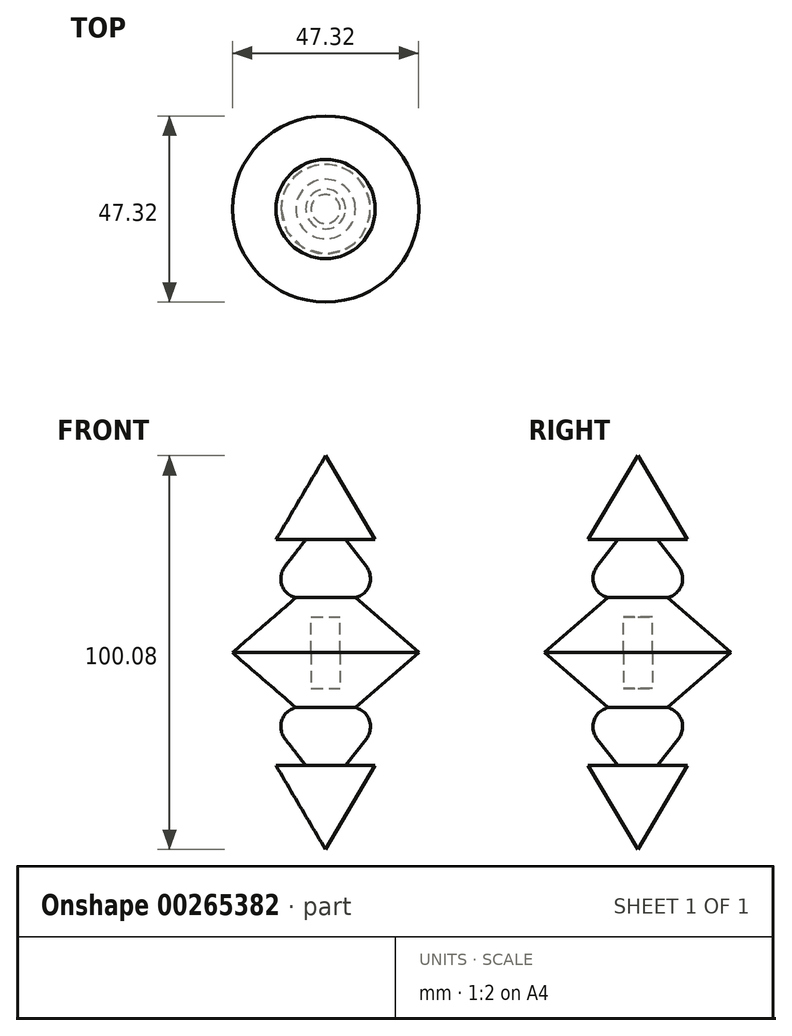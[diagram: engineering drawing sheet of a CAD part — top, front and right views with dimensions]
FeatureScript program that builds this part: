
annotation { "Feature Type Name" : "Feature", "Feature Type Description" : "" }
export const myFeature = defineFeature(function(context is Context, id is Id, definition is map)
    precondition{}
    {
        {
            var Q0;
            Q0=qCreatedBy(makeId("Front.planeOp"),FACE);
            var sketch = newSketch(context, id + "F0", { "sketchPlane" : qUnion([Q0])});
            skLineSegment(sketch, "E0", {"start": v(0, 50.04) * mm, "end": v(12.6, 28.7) * mm});
            skLineSegment(sketch, "E1", {"start": v(12.6, 28.7) * mm, "end": v(5.04, 28.7) * mm});
            skLineSegment(sketch, "E2", {"start": v(5.04, 28.7) * mm, "end": v(16.49, 13.97) * mm});
            skLineSegment(sketch, "E3", {"start": v(16.49, 13.97) * mm, "end": v(7.56, 13.97) * mm});
            skLineSegment(sketch, "E4", {"start": v(7.56, 13.97) * mm, "end": v(23.66, 0) * mm});
            skLineSegment(sketch, "E5", {"start": v(23.66, 0) * mm, "end": v(3.69, 0) * mm});
            skLineSegment(sketch, "E6", {"start": v(3.69, 0) * mm, "end": v(3.69, -9.12) * mm});
            skLineSegment(sketch, "E7", {"start": v(3.69, -9.12) * mm, "end": v(0, -9.12) * mm});
            skLineSegment(sketch, "E8", {"start": v(0, -9.12) * mm, "end": v(0, 50.04) * mm});
            skPoint(sketch, "E9.orphan", {"position": v(0, 0) * mm});
            skSolve(sketch);
        }
        {
            var Q0;
            Q0 = qSketchRegion(id + "F0", true);
            var Q1;
            Q1=sQuery(id+"F0.wireOp",EDGE,"E8");
            revolve(context, id + "F1", {"entities" : qUnion([Q0]), "axis" : qUnion([Q1]), "revolveType" : RevolveType.FULL});
        }
        {
            var Q0;
            Q0=makeQuery(id+"F1.opRevolve","SWEPT_BODY",BODY,{"disambiguationData":[OSD([sQuery(id+"F0.wireOp",EDGE,"E0"),sQuery(id+"F0.wireOp",EDGE,"E1"),sQuery(id+"F0.wireOp",EDGE,"E2"),sQuery(id+"F0.wireOp",EDGE,"E3"),sQuery(id+"F0.wireOp",EDGE,"E4"),sQuery(id+"F0.wireOp",EDGE,"E5"),sQuery(id+"F0.wireOp",EDGE,"E6"),sQuery(id+"F0.wireOp",EDGE,"E7"),sQuery(id+"F0.wireOp",EDGE,"E8")])]});
            var Q1;
            Q1=qCreatedBy(makeId("Top.planeOp"),FACE);
            mirror(context, id + "F2", {"entities" : qUnion([Q0]), "mirrorPlane" : qUnion([Q1])});
        }
        {
            var Q0;
            Q0=makeQuery(id+"F1.opRevolve","SWEPT_EDGE",EDGE,{"disambiguationData":[OSD([sQuery(id+"F0.wireOp",EDGE,"E2"),sQuery(id+"F0.wireOp",EDGE,"E3")])]});
            fillet(context, id + "F3", {"entities" : qUnion([Q0]), "radius" : 5 * mm, "tangentPropagation" : true, "allowEdgeOverflow" : false});
        }
        {
            var Q0;
            Q0=makeQuery(id+"F2.opPattern","COPY",EDGE,{"derivedFrom":makeQuery(id+"F1.opRevolve","SWEPT_EDGE",EDGE,{"disambiguationData":[OSD([sQuery(id+"F0.wireOp",EDGE,"E2"),sQuery(id+"F0.wireOp",EDGE,"E3")])]}),"instanceName":"1"});
            fillet(context, id + "F4", {"entities" : qUnion([Q0]), "radius" : 5 * mm, "tangentPropagation" : true, "allowEdgeOverflow" : false});
        }
    });
